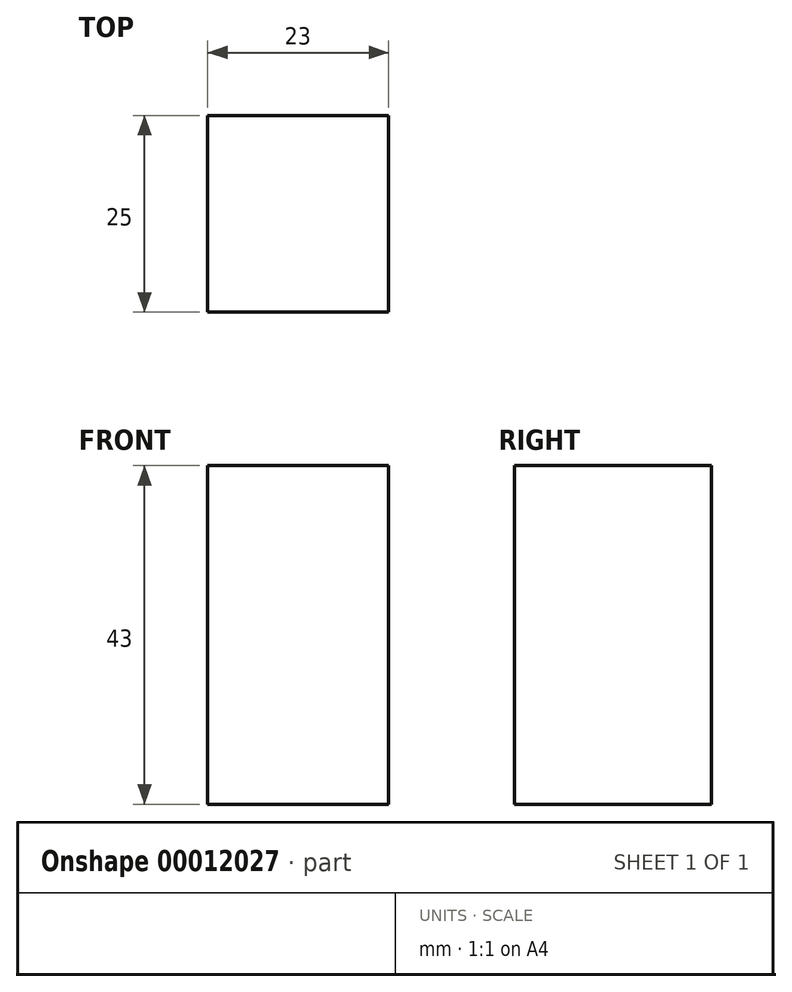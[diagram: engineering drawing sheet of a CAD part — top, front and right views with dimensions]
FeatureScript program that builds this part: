
annotation { "Feature Type Name" : "Feature", "Feature Type Description" : "" }
export const myFeature = defineFeature(function(context is Context, id is Id, definition is map)
    precondition{}
    {
        {
            var Q0;
            Q0=qCreatedBy(makeId("Top.planeOp"),FACE);
            var sketch = newSketch(context, id + "F0", { "sketchPlane" : qUnion([Q0])});
            skLineSegment(sketch, "E0.rect.bottom", {"start": v(11.5, 12.5) * mm, "end": v(-11.5, 12.5) * mm});
            skLineSegment(sketch, "E0.rect.top", {"start": v(11.5, -12.5) * mm, "end": v(-11.5, -12.5) * mm});
            skLineSegment(sketch, "E0.rect.left", {"start": v(11.5, 12.5) * mm, "end": v(11.5, -12.5) * mm});
            skLineSegment(sketch, "E0.rect.right", {"start": v(-11.5, 12.5) * mm, "end": v(-11.5, -12.5) * mm});
            skPoint(sketch, "E0.rect.middle", {"position": v(0, 0) * mm});
            skSolve(sketch);
        }
        {
            var Q0;
            Q0 = qSketchRegion(id + "F0", true);
            extrude(context, id + "F1", {"entities" : qUnion([Q0]), "depth" : 43 * mm});
        }
    });
